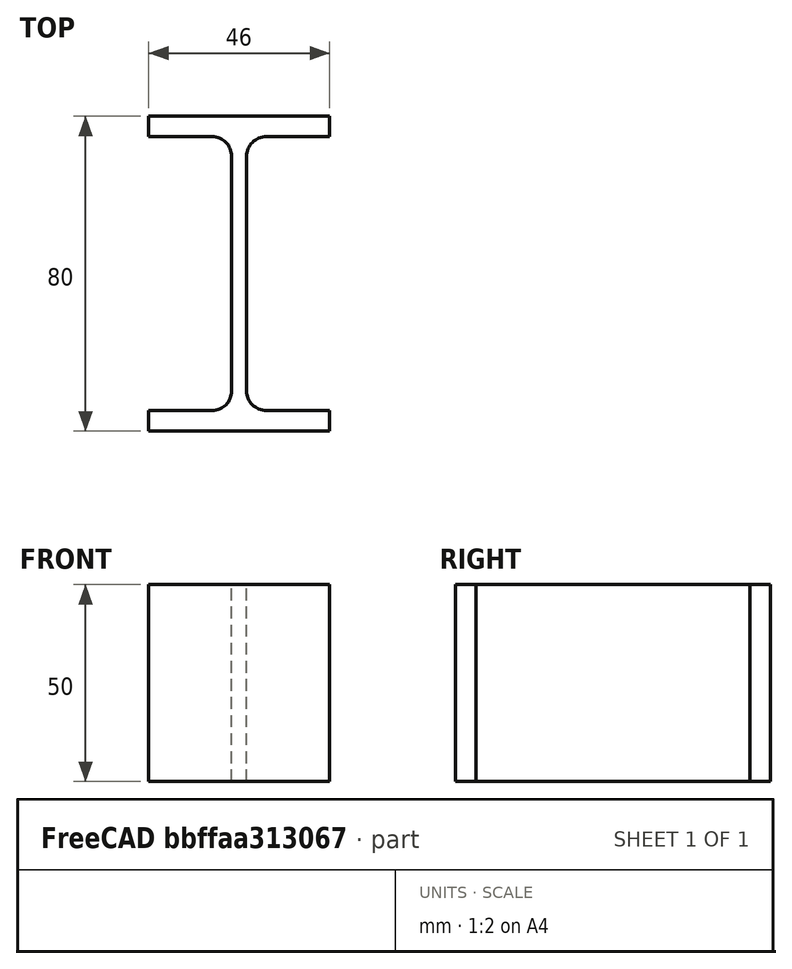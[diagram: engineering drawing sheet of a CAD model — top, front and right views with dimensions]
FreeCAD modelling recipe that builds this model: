
FCSTD DOCUMENT  (FreeCAD 0.15R4671 (Git))
Label: IPE-Profile 80 DIN1025-5 S235JR
License: All rights reserved
LicenseURL: http://en.wikipedia.org/wiki/All_rights_reserved
objects: Sketcher::SketchObject×1, Part::Extrusion×1
note: 2 computed .brp shape members not serialized (recipe doc carries the construction recipe); baked Part::Feature solids carry a one-line shape summary decoded from their .brp

FEATURE [Sketcher::SketchObject] Sketch
  sketch-geometry (16):
    g0: LineSegment StartX=1.9 StartY=-29.8 StartZ=0 EndX=1.9 EndY=29.8 EndZ=0
    g1: LineSegment StartX=6.9 StartY=34.8 StartZ=0 EndX=23 EndY=34.8 EndZ=0
    g2: LineSegment StartX=23 StartY=34.8 StartZ=0 EndX=23 EndY=40 EndZ=0
    g3: LineSegment StartX=23 StartY=40 StartZ=0 EndX=-23 EndY=40 EndZ=0
    g4: LineSegment StartX=-23 StartY=40 StartZ=0 EndX=-23 EndY=34.8 EndZ=0
    g5: LineSegment StartX=-23 StartY=34.8 StartZ=0 EndX=-6.9 EndY=34.8 EndZ=0
    g6: LineSegment StartX=-1.9 StartY=29.8 StartZ=0 EndX=-1.9 EndY=-29.8 EndZ=0
    g7: LineSegment StartX=-6.9 StartY=-34.8 StartZ=0 EndX=-23 EndY=-34.8 EndZ=0
    g8: LineSegment StartX=-23 StartY=-34.8 StartZ=0 EndX=-23 EndY=-40 EndZ=0
    g9: LineSegment StartX=-23 StartY=-40 StartZ=0 EndX=23 EndY=-40 EndZ=0
    g10: LineSegment StartX=23 StartY=-40 StartZ=0 EndX=23 EndY=-34.8 EndZ=0
    g11: LineSegment StartX=23 StartY=-34.8 StartZ=0 EndX=6.9 EndY=-34.8 EndZ=0
    g12: ArcOfCircle CenterX=6.9 CenterY=29.8 CenterZ=0 NormalX=0 NormalY=0 NormalZ=1 Radius=5 StartAngle=1.5708 EndAngle=3.14159
    g13: ArcOfCircle CenterX=6.9 CenterY=-29.8 CenterZ=0 NormalX=0 NormalY=0 NormalZ=1 Radius=5 StartAngle=3.14159 EndAngle=4.71239
    g14: ArcOfCircle CenterX=-6.9 CenterY=29.8 CenterZ=0 NormalX=0 NormalY=0 NormalZ=1 Radius=5 StartAngle=0 EndAngle=1.5708
    g15: ArcOfCircle CenterX=-6.9 CenterY=-29.8 CenterZ=0 NormalX=0 NormalY=0 NormalZ=1 Radius=5 StartAngle=4.71239 EndAngle=6.28319
  constraints (42):
    c: Vertical(g0)
    c: Coincident(g2,g1)
    c: Vertical(g2)
    c: Coincident(g3,g2)
    c: Coincident(g4,g3)
    c: Vertical(g4)
    c: Coincident(g5,g4)
    c: Horizontal(g5)
    c: Vertical(g6)
    c: Horizontal(g7)
    c: Coincident(g8,g7)
    c: Vertical(g8)
    c: Coincident(g9,g8)
    c: Horizontal(g9)
    c: Coincident(g10,g9)
    c: Vertical(g10)
    c: Coincident(g11,g10)
    c: Horizontal(g11)
    c: Tangent(g1,g12) = 1.5708
    c: Tangent(g0,g12) = 1.5708
    c: Tangent(g0,g13) = 1.5708
    c: Tangent(g11,g13) = 1.5708
    c: Tangent(g5,g14) = 1.5708
    c: Tangent(g6,g14) = 1.5708
    c: Tangent(g6,g15) = 1.5708
    c: Tangent(g7,g15) = 1.5708
    c: Equal(g3,g9)
    c: Equal(g2,g4)
    c: Equal(g4,g8)
    c: Equal(g8,g10)
    c: Equal(g12,g14)
    c: Equal(g14,g15)
    c: Equal(g15,g13)
    c: Symmetric(g2,g3,g-2)
    c: Symmetric(g9,g8,g-2)
    c: Symmetric(g0,g6,g-2)
    c: Symmetric(g2,g9,g-1)
    c: DistanceY(g2,g9) = -80
    c: DistanceX(g3) = -46
    c: DistanceX(g0,g6) = -3.8
    c: DistanceY(g2) = 5.2
    c: Radius(g12) = 5
FEATURE [Part::Extrusion] Extrude  label="IPE-Profile 80 DIN1025-5 S235JR"
  Base = -> Sketch
  Dir = (0,0,50)
  Solid = true
